# Revit family: ROSENBERG_Z_G
name_source: partatom
category: Wyposażenie mechaniczne
revit_build: Autodesk Revit 2017 (Build: 20160225_1515(x64)
units: mm (PartAtom-declared; Revit-internal decimal feet)

## family parameters
Numer OmniClass = 23.75.00.00
Oparty na płaszczyźnie roboczej = Nie
Punkt obliczania pomieszczeń = Nie
Tnij formami wycięć po wczytaniu = Nie
Typ części = Dzieli na
Tytuł OmniClass = Climate Control (HVAC)
Współdzielony = Nie
Wymiar okrągłego złącza = Użyj średnicy
Zawsze pionowo = Tak

## types (14) — shared parameters
Date = 10.2018
Frequency = 50 Hz
Materiał = <Wg kategorii>
Opis = Tube fan
Producent = Rosenberg
Protection Class = IP44
URL = https://www.rosenberg.pl
Version = 1
Voltage = 230 V

## per-type parameters (varying)
| type | Air_flow | Current | Diameter_connector | Diameter_hole | Height | Length | Length_box | Power | Pressure | Weight | Width | X_connector | Y_connector | b1 | f1 |
| 355 G.4EA R | 1209.0 m³/h | 1 A | 355 mm | 349 mm | 460 mm | 700 mm | 600 mm | 290 W | 294.0 Pa | 44.00 kg | 620 mm | 230 mm | 310 mm | 175 mm | 467 mm |
| 315 G.3DI R | 1019.0 m³/h | 1 A | 315 mm | 309 mm | 420 mm | 680 mm | 580 mm | 165 W | 214.0 Pa | 28.70 kg | 595 mm | 298 mm | 208 mm | 170 mm | 453 mm |
| 250 G.3BK R | 606.0 m³/h | 1 A | 250 mm  [stored 0.82021 ft] | 244 mm | 354 mm | 520 mm | 420 mm | 157 W | 365.0 Pa | 18.40 kg | 465 mm | 233 mm | 180 mm | 130 mm | 347 mm |
| 400 G.4EA R | 1697.0 m³/h | 2 A | 400 mm | 394 mm | 470 mm | 750 mm | 650 mm | 420 W | 355.0 Pa | 40.00 kg | 645 mm | 323 mm | 242 mm | 188 mm | 500 mm |
| 315 G.4EA E2 | 1029.0 m³/h | 1 A | 315 mm | 309 mm | 420 mm | 680 mm | 580 mm | 300 W | 467.0 Pa | 35.00 kg | 595 mm | 210 mm | 228 mm | 170 mm | 453 mm |
| 355 G.4EA E2 | 1147.0 m³/h | 2 A | 355 mm | 349 mm | 420 mm | 680 mm | 580 mm | 360 W | 498.0 Pa | 40.00 kg | 595 mm | 230 mm | 228 mm | 170 mm | 453 mm |
| 200 G.3BK E1 | 413.0 m³/h | 1 A | 200 mm  [stored 0.656168 ft] | 194 mm | 314 mm | 490 mm | 390 mm | 160 W | 408.0 Pa | 14.40 kg | 365 mm | 183 mm | 200 mm  [stored 0.656168 ft] | 123 mm | 327 mm |
| 160 G.3BK E1 | 280.0 m³/h | 1 A | 160 mm | 154 mm | 282 mm | 460 mm | 360 mm | 120 W | 256.0 Pa | 9.40 kg | 344 mm | 172 mm | 185 mm | 115 mm | 307 mm |
| 125 G.3BK E1 | 211.0 m³/h | 0 A | 125 mm  [stored 0.410105 ft] | 119 mm | 260 mm | 460 mm | 360 mm | 65 W | 309.0 Pa | 12.40 kg | 340 mm | 170 mm | 170 mm | 115 mm | 307 mm |
| 125 G.3BK R | 249.0 m³/h | 1 A | 125 mm  [stored 0.410105 ft] | 119 mm | 244 mm | 460 mm | 360 mm | 103 W | 402.0 Pa | 13.50 kg | 380 mm | 190 mm | 105 mm | 115 mm | 307 mm |
| 160 G.3BK R | 294.0 m³/h | 1 A | 160 mm | 154 mm | 264 mm | 460 mm | 360 mm | 110 W | 381.0 Pa | 14.00 kg | 380 mm | 190 mm | 125 mm  [stored 0.410105 ft] | 115 mm | 307 mm |
| 200 G.3BK R | 432.0 m³/h | 1 A | 200 mm  [stored 0.656168 ft] | 194 mm | 314 mm | 490 mm | 390 mm | 127 W | 384.0 Pa | 16.80 kg | 420 mm | 210 mm | 150 mm | 123 mm | 327 mm |
| 250 G.3DI E2 | 751.0 m³/h | 1 A | 250 mm  [stored 0.82021 ft] | 244 mm | 315 mm | 490 mm | 390 mm | 220 W | 333.0 Pa | 17.40 kg | 465 mm | 233 mm | 175 mm | 123 mm | 327 mm |
| 400 G.5FA E2 | 1410.0 m³/h | 3 A | 400 mm | 394 mm | 475 mm | 750 mm | 650 mm | 600 W | 667.0 Pa | 40.00 kg | 645 mm | 250 mm  [stored 0.82021 ft] | 250 mm  [stored 0.82021 ft] | 188 mm | 500 mm |

note: column(s) folded — value = type name in every type: Model

note: [stored X ft] marks values corroborated as IEEE doubles in the binary element streams (Revit-internal decimal feet)

## geometry (parser evidence)
native form markers: Blend x2, Sweep x2
no freeform markers — native parametric forms only
